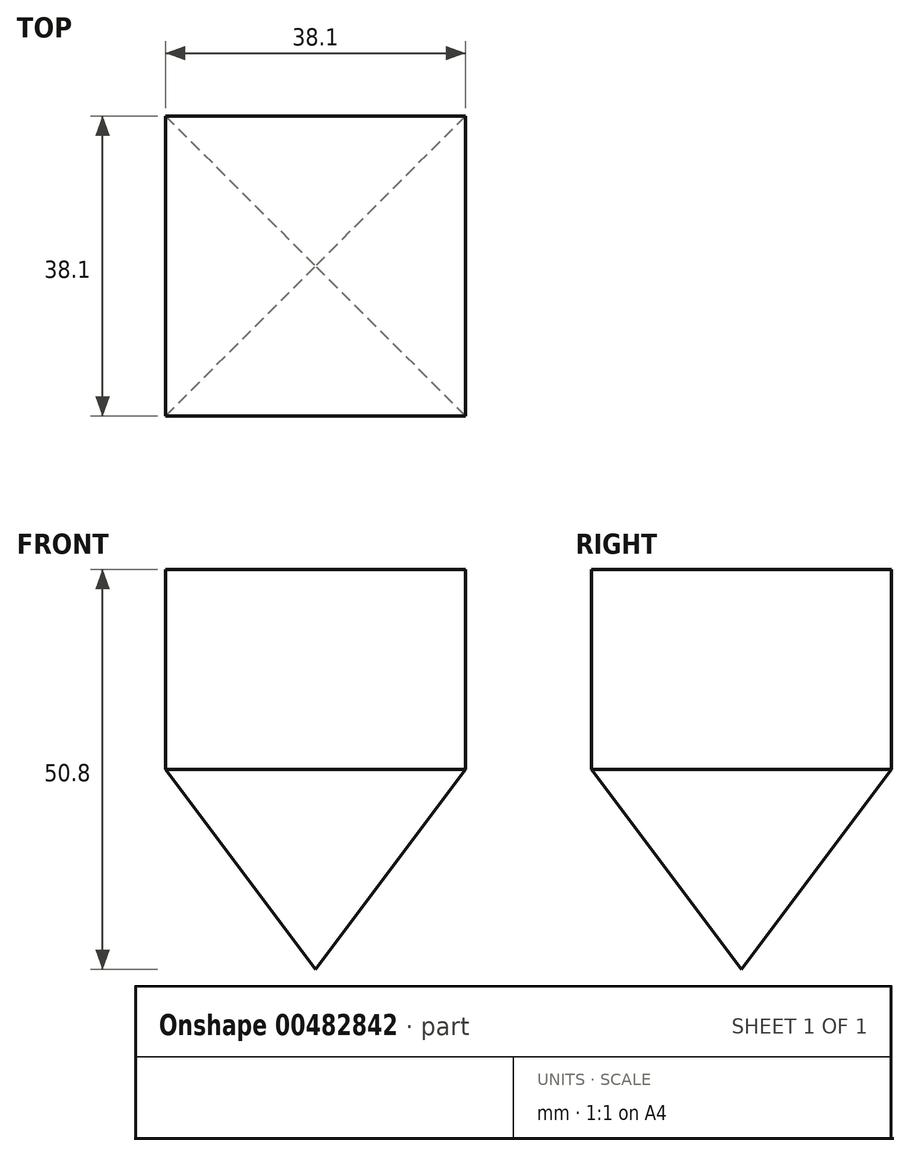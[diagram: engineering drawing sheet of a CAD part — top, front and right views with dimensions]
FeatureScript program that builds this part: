
annotation { "Feature Type Name" : "Feature", "Feature Type Description" : "" }
export const myFeature = defineFeature(function(context is Context, id is Id, definition is map)
    precondition{}
    {
        {
            var Q0;
            Q0=qCreatedBy(makeId("Top.planeOp"),FACE);
            var sketch = newSketch(context, id + "F0", { "sketchPlane" : qUnion([Q0])});
            skLineSegment(sketch, "E0.bottom", {"start": v(-19.05, 19.05) * mm, "end": v(19.05, 19.05) * mm});
            skLineSegment(sketch, "E0.top", {"start": v(-19.05, -19.05) * mm, "end": v(19.05, -19.05) * mm});
            skLineSegment(sketch, "E0.left", {"start": v(-19.05, 19.05) * mm, "end": v(-19.05, -19.05) * mm});
            skLineSegment(sketch, "E0.right", {"start": v(19.05, 19.05) * mm, "end": v(19.05, -19.05) * mm});
            skSolve(sketch);
        }
        {
            var Q0;
            Q0 = qSketchRegion(id + "F0", true);
            extrude(context, id + "F1", {"entities" : qUnion([Q0]), "depth" : 50.8 * mm});
        }
        {
            var Q0;
            Q0=makeQuery(id+"F1.opExtrude","CAP_FACE",FACE,{"disambiguationData":[OSD([sQuery(id+"F0.wireOp",EDGE,"E0.bottom"),sQuery(id+"F0.wireOp",EDGE,"E0.top"),sQuery(id+"F0.wireOp",EDGE,"E0.left"),sQuery(id+"F0.wireOp",EDGE,"E0.right")])],"isStart":true});
            chamfer(context, id + "F2", {"entities" : qUnion([Q0]), "chamferType" : ChamferType.TWO_OFFSETS, "width1" : 19.05 * mm, "oppositeDirection" : false, "width2" : 25.4 * mm, "tangentPropagation" : true});
        }
    });
